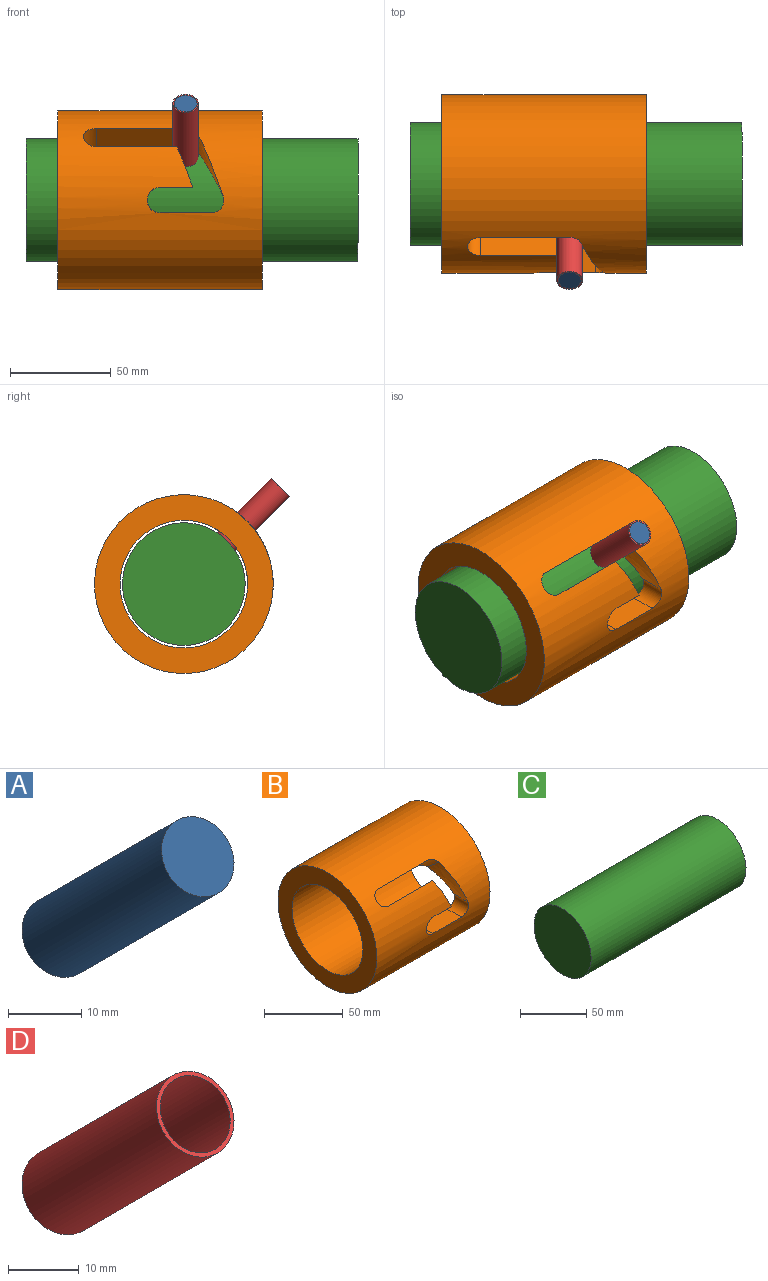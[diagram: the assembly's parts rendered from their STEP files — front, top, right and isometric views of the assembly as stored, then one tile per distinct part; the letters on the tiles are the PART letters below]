
ASSEMBLY  parts=4 mates=2
PART A: 3 faces, bbox 11.4x35x35 mm
  f0: cylinder r=5.71mm len=35.02mm, axis (0,0.71,-0.71), area 1368.1mm2, adj f1,f2
  f1: plane 11.43x8.08mm, normal (0,-0.71,0.71), area 102.6mm2, adj f0
  f2: plane 11.43x8.08mm, normal (0,0.71,-0.71), area 102.6mm2, adj f0
PART B: 14 faces, bbox 102.2x89.6x89.5 mm
  f0: cylinder r=31.75mm len=101.6mm, axis (1,0,0), area 18924.1mm2, adj f2,f3,f4,f5,f6,f7,f8,f9
  f1: cylinder r=44.45mm len=101.6mm, axis (-1,0,0), area 26935.2mm2, adj f2,f3,f4,f5,f6,f7,f8,f9
  f2: plane 88.9x88.9mm, normal (1,0,0), area 3040.2mm2, adj f0,f1
  f3: plane 88.9x88.9mm, normal (-1,0,0), area 3040.2mm2, adj f0,f1
  f4: plane 16.91x13.47mm, normal (0,0,-1), area 203mm2, adj f0,f1,f5,f13
  f5: cylinder r=6.35mm len=12.89mm, axis (0,1,0), area 257.1mm2, adj f0,f1,f4,f6
  f6: plane 25.4x12.89mm, normal (0,0,1), area 327.3mm2, adj f0,f1,f5,f7
  f7: cylinder r=6.35mm len=13.29mm, axis (0,1,0), area 164.2mm2, adj f0,f1,f6,f12
  f8: plane 44.45x9.11mm, normal (0,-0.71,-0.71), area 572.8mm2, adj f0,f1,f9,f11
  f9: cylinder r=6.35mm len=18.09mm, axis (0,0.71,-0.71), area 257.1mm2, adj f0,f1,f8,f10
  f10: plane 40.73x9.27mm, normal (0,0.71,0.71), area 518.9mm2, adj f0,f1,f9,f13
  f11: cylinder r=6.35mm len=12.47mm, axis (0,0.71,-0.71), area 98.3mm2, adj f0,f1,f8,f12
  f12: bspline ~30.84x24.2mm, area 412.3mm2, adj f0,f1,f7,f11
  f13: bspline ~31.67x20.19mm, area 233.6mm2, adj f0,f1,f4,f10
PART C: 3 faces, bbox 165.1x61x61 mm
  f0: plane 60.96x60.96mm, normal (-1,0,0), area 2918.6mm2, adj f2
  f1: plane 60.96x60.96mm, normal (1,0,0), area 2918.6mm2, adj f2
  f2: cylinder r=30.48mm len=165.1mm, axis (-1,0,0), area 31618.5mm2, adj f0,f1
PART D: 4 faces, bbox 12.7x35.9x35.9 mm
  f0: cylinder r=5.71mm len=35.02mm, axis (0,0.71,-0.71), area 1368.1mm2, adj f2,f3
  f1: cylinder r=6.35mm len=35.92mm, axis (0,0.71,-0.71), area 1520.1mm2, adj f2,f3
  f2: plane 12.7x8.98mm, normal (0,-0.71,0.71), area 24.1mm2, adj f0,f1
  f3: plane 12.7x8.98mm, normal (0,0.71,-0.71), area 24.1mm2, adj f0,f1
PLACE A rot(axis=(-1,0,0),0deg) t=(44.44,0,0)mm
PLACE B at identity fixed
PLACE C rot(axis=(-1,0,0),0deg) t=(44.44,0,0)mm
PLACE D rot(axis=(-1,0,0),0deg) t=(44.44,0,0)mm
MATE cylindrical B.f1 <-> C.f2  axis (-1,0,0) through (-50.8,0,0)mm
MATE fastened A.f0 <-> D.f0  axis (0,-0.71,0.71) through (12.69,-48.04,48.08)mm
